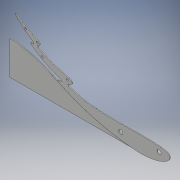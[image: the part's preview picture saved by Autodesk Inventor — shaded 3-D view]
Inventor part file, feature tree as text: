
AUTODESK INVENTOR PART (.ipt)
format: ipt  version: 2018 (Build 220112000, 112)  size: 203,776 bytes
history: native  units: mm
features: projected_geometry x2, extrude x1, sketch x1
ambient origin geometry x8: Origin, YZ Plane, XZ Plane, XY Plane, X Axis, Y Axis, Z Axis, Center Point
bodies: Body1 (feature_tree)
feature tree (4):
  extrude  "押し出し1"  Depth=2.0mm TaperAngle=0.0deg
  sketch  "スケッチ1"
  projected_geometry  "投影ループ2"
  projected_geometry  "投影ループ3"
